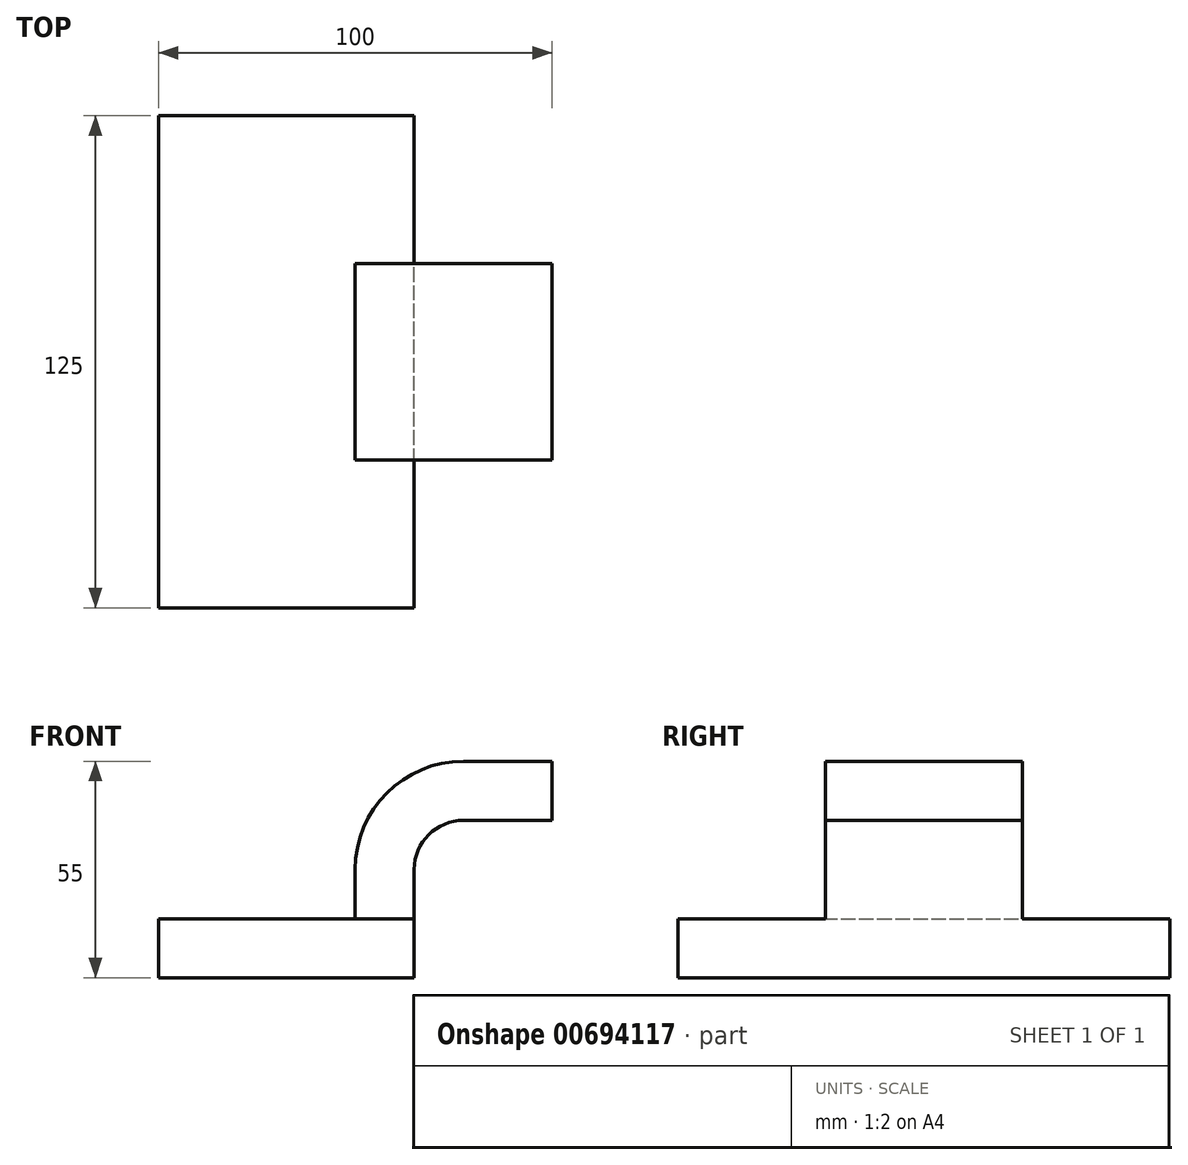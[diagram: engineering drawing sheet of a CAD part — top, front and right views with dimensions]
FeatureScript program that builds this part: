
annotation { "Feature Type Name" : "Feature", "Feature Type Description" : "" }
export const myFeature = defineFeature(function(context is Context, id is Id, definition is map)
    precondition{}
    {
        {
            var Q0;
            Q0=qCreatedBy(makeId("Front.planeOp"),FACE);
            var sketch = newSketch(context, id + "F0", { "sketchPlane" : qUnion([Q0])});
            skLineSegment(sketch, "E0.bottom", {"start": v(-32.5, 7.5) * mm, "end": v(32.5, 7.5) * mm});
            skLineSegment(sketch, "E0.top", {"start": v(-32.5, -7.5) * mm, "end": v(32.5, -7.5) * mm});
            skLineSegment(sketch, "E0.left", {"start": v(-32.5, 7.5) * mm, "end": v(-32.5, -7.5) * mm});
            skLineSegment(sketch, "E0.right", {"start": v(32.5, 7.5) * mm, "end": v(32.5, -7.5) * mm});
            skPoint(sketch, "E0.middle", {"position": v(0, 0) * mm});
            skLineSegment(sketch, "E1.bottom", {"start": v(47.5, 30) * mm, "end": v(87.5, 30) * mm});
            skLineSegment(sketch, "E1.top", {"start": v(47.5, 52.5) * mm, "end": v(87.5, 52.5) * mm});
            skLineSegment(sketch, "E1.left", {"start": v(47.5, 30) * mm, "end": v(47.5, 52.5) * mm});
            skLineSegment(sketch, "E1.right", {"start": v(87.5, 30) * mm, "end": v(87.5, 52.5) * mm});
            skLineSegment(sketch, "E2", {"start": v(32.5, 7.5) * mm, "end": v(32.5, 20) * mm});
            skArc(sketch, "E3", {"start": v(32.5, 20) * mm, "mid": v(36.16, 28.84) * mm, "end": v(45, 32.5) * mm});
            skPoint(sketch, "E4.endSnap0", {"position": v(67.5, 30) * mm});
            skLineSegment(sketch, "E5", {"start": v(45, 32.5) * mm, "end": v(67.5, 32.5) * mm});
            skLineSegment(sketch, "E6.0", {"start": v(45, 47.5) * mm, "end": v(67.5, 47.5) * mm});
            skArc(sketch, "E6.1", {"start": v(17.5, 20) * mm, "mid": v(25.55, 39.45) * mm, "end": v(45, 47.5) * mm});
            skLineSegment(sketch, "E6.2", {"start": v(17.5, 7.5) * mm, "end": v(17.5, 20) * mm});
            skLineSegment(sketch, "E7", {"start": v(67.5, 30) * mm, "end": v(67.5, 52.5) * mm});
            skFitSpline(sketch, "E8", {"points": [v(-32.5, 7.5) * mm, v(45, 47.5) * mm], "startDerivative": vector(0, 57.16) * mm, "endDerivative": vector(112.3, 0) * mm});
            skSolve(sketch);
        }
        {
            var Q0;
            Q0=makeQuery(id+"F0.imprint","IMPRINT",FACE,{"disambiguationData":[TD([[makeQuery(id+"F0.imprint","IMPRINT",EDGE,{"derivedFrom":sQuery(id+"F0.wireOp",EDGE,"E0.top")}),1.0]])]});
            extrude(context, id + "F1", {"entities" : qUnion([Q0]), "endBound" : BoundingType.SYMMETRIC, "depth" : 125 * mm, "offsetDistance" : 25 * mm});
        }
        {
            var Q0;
            {var subQ1=sQuery(id+"F0.wireOp",EDGE,"E2");Q0=makeQuery(id+"F0.imprint","IMPRINT",FACE,{"disambiguationData":[TD([[makeQuery(id+"F0.imprint","IMPRINT",EDGE,{"derivedFrom":subQ1}),1.0]])]});}
            var Q1;
            {var subQ0=sQuery(id+"F0.wireOp",EDGE,"E5");var subQ1=sQuery(id+"F0.wireOp",EDGE,"E1.left");var subQ2=makeQuery(id+"F0.imprint","INTERSECT",VERTEX,{"derivedFrom":[subQ1,subQ0]});Q1=makeQuery(id+"F0.imprint","IMPRINT",FACE,{"disambiguationData":[TD([[makeQuery(id+"F0.imprint","IMPRINT",EDGE,{"disambiguationData":[TD([[subQ2,-1.0]])],"derivedFrom":subQ1}),-1.0]])]});}
            extrude(context, id + "F2", {"entities" : qUnion([Q0, Q1]), "operationType" : NewBodyOperationType.ADD, "endBound" : BoundingType.SYMMETRIC, "depth" : 50 * mm, "offsetDistance" : 25 * mm});
        }
        {
            var Q0;
            Q0=makeQuery(id+"F0.imprint","IMPRINT",FACE,{"disambiguationData":[TD([[makeQuery(id+"F0.imprint","IMPRINT",EDGE,{"derivedFrom":sQuery(id+"F0.wireOp",EDGE,"E6.1")}),1.0]])]});
            extrude(context, id + "F3", {"entities" : qUnion([Q0]), "operationType" : NewBodyOperationType.ADD, "endBound" : BoundingType.SYMMETRIC, "depth" : 12.5 * mm, "offsetDistance" : 25 * mm});
        }
    });
